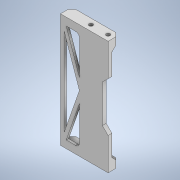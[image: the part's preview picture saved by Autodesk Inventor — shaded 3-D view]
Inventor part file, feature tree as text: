
AUTODESK INVENTOR PART (.ipt)
format: ipt  version: 2021 (Build 250183000, 183)  size: 268,288 bytes
history: native  units: mm
features: sketch x11, extrude x9, chamfer x6, hole x2, fillet x1
ambient origin geometry x8: Origin, YZ Plane, XZ Plane, XY Plane, X Axis, Y Axis, Z Axis, Center Point
bodies: Solid1 (feature_tree)
feature tree (29):
  extrude  "Extrusion1"  Depth=15.0mm
  extrude  "Extrusion2"  Depth=6.0mm
  extrude  "Extrusion3"  Depth=3.0mm TaperAngle=0.0deg
  chamfer  "Chamfer1"  Distance=3.0mm Angle=45.0deg
  hole  "Hole1"  [1 undecoded]
  hole  "Hole2"  [1 undecoded]
  extrude  "Extrusion4"  Depth=3.0mm
  chamfer  "Chamfer2"  Distance=30.0mm
  chamfer  "Chamfer3"  Distance=2.0mm Angle=45.0deg
  extrude  "Extrusion5"  Depth=3.0mm
  chamfer  "Chamfer4"  Distance=2.0mm
  extrude  "Extrusion6"  Depth=3.0mm TaperAngle=45.0deg
  chamfer  "Chamfer5"  Distance=10.0mm
  extrude  "Extrusion7"  Depth=1.2mm TaperAngle=0.0deg
  chamfer  "Chamfer6"  Distance=0.8mm Angle=45.0deg
  extrude  "Extrusion8"  Depth=2.0mm
  fillet  "Fillet1"  Radius=2.0mm
  extrude  "Extrusion10"  Depth=4.8mm TaperAngle=0.0deg
  sketch  "Sketch1"  dims[d0=15.0mm d1=60.0mm]
  sketch  "Sketch2"  dims[d2=2.0mm d3=0.0mm d4=6.0mm]
  sketch  "Sketch3"  dims[d5=3.0mm d6=0.0mm d7=3.0mm d8=0.0mm d9=3.0mm d10=2.0mm d11=45.0deg]
  sketch  "Sketch4"  dims[d12=3.0mm d13=12.0mm]
  sketch  "Sketch5"  dims[d14=3.0mm d15=3.0mm]
  sketch  "Sketch6"  dims[d16=2.0mm d17=6.0mm d18=4.0mm d19=2.0mm d20=90.0deg d21=3.0mm d22=20.594885mm]
  sketch  "Sketch7"  dims[d23=2.0mm d24=6.0mm d25=4.0mm d26=2.0mm d27=90.0deg d28=3.0mm d29=20.594885mm d30=0.1mm]
  sketch  "Sketch8"  dims[d31=0.1mm d32=30.0mm d33=0.0mm d34=2.0mm d35=2.0mm d36=45.0deg]
  sketch  "Sketch9"  dims[d37=2.0mm d38=2.0mm d39=45.0deg d40=3.0mm]
  sketch  "Sketch10"  dims[d41=20.0mm]
  sketch  "Sketch12"  dims[d42=20.0mm d43=2.0mm d44=0.0mm d45=3.0mm d46=2.0mm d47=45.0deg d48=10.0mm d49=1.2mm d50=0.0mm d51=0.8mm d52=2.0mm d53=45.0deg d54=2.0mm d55=2.0mm d56=4.8mm d57=0.0mm d58=2.0mm d59=2.0mm d60=45.0deg d61=2.0mm d62=2.0mm d63=2.0mm d64=2.0mm d65=0.0mm d70=2.0mm d71=1.0mm d72=51.8mm d73=25.9mm d74=2.0mm d75=2.0mm d76=1.2mm d77=0.0mm d78=0.5mm d79=0.872665mm]
note: 2 required parameter values undecoded (feature->parameter linkage not recoverable at this tier; creation-order binding heuristic only, values carry confidence <= 0.55)
